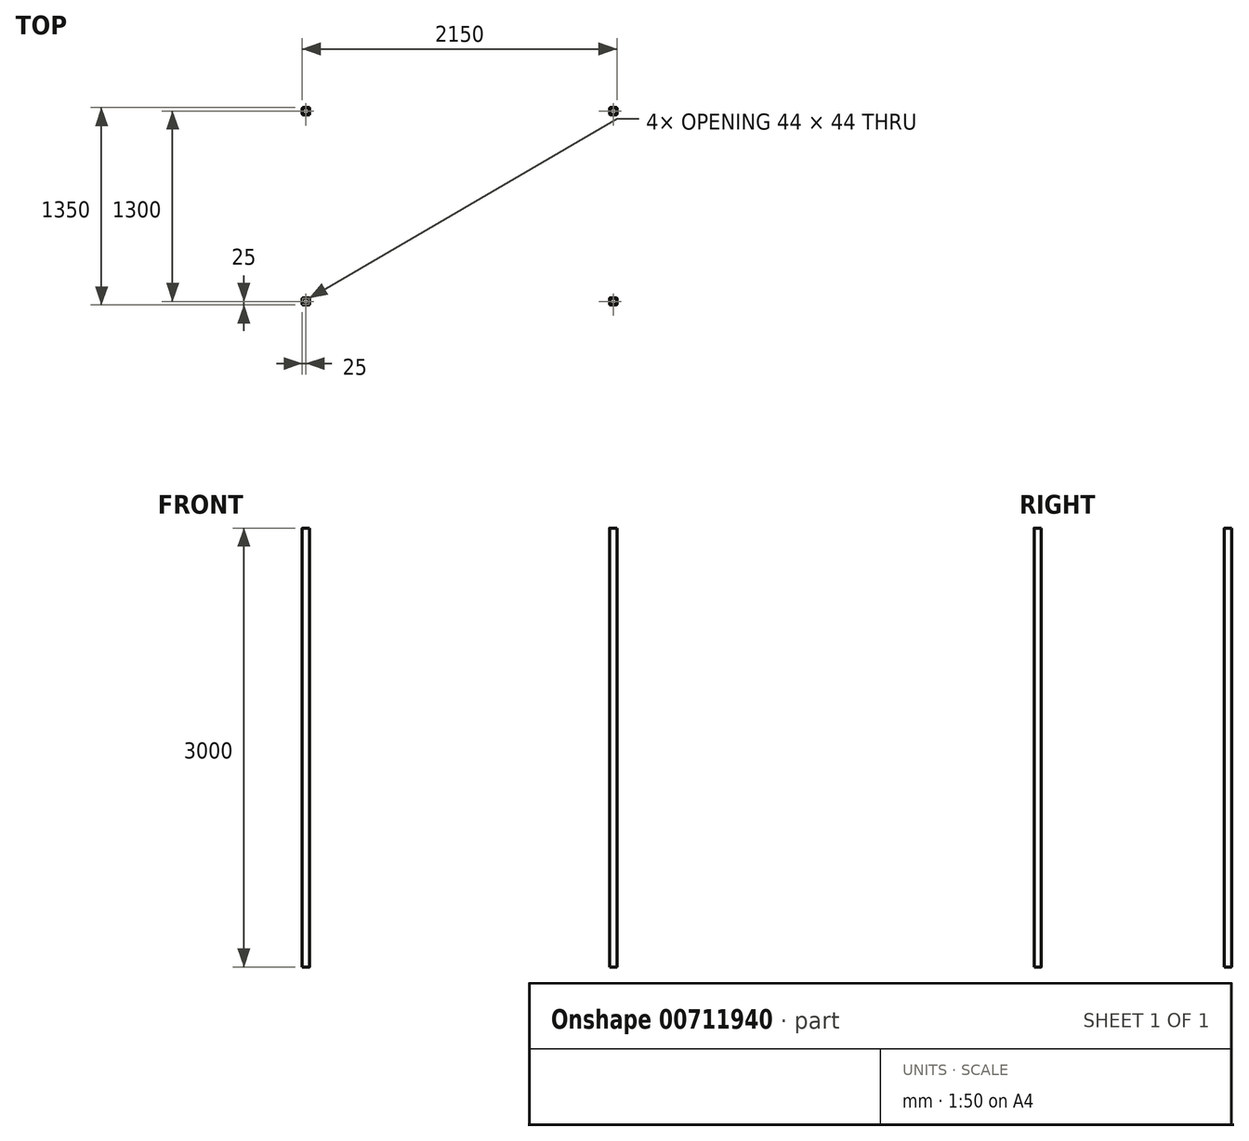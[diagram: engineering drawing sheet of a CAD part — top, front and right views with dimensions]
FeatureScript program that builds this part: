
annotation { "Feature Type Name" : "Feature", "Feature Type Description" : "" }
export const myFeature = defineFeature(function(context is Context, id is Id, definition is map)
    precondition{}
    {
        {
            var Q0;
            Q0=qCreatedBy(makeId("Top.planeOp"),FACE);
            var sketch = newSketch(context, id + "F0", { "sketchPlane" : qUnion([Q0])});
            skLineSegment(sketch, "E0.bottom", {"start": v(-1045, 1350) * mm, "end": v(-1005, 1350) * mm});
            skLineSegment(sketch, "E0.top", {"start": v(-1045, 1300) * mm, "end": v(-1005, 1300) * mm});
            skLineSegment(sketch, "E0.left", {"start": v(-1050, 1345) * mm, "end": v(-1050, 1305) * mm});
            skLineSegment(sketch, "E0.right", {"start": v(-1000, 1345) * mm, "end": v(-1000, 1305) * mm});
            skPoint(sketch, "E1.visualSharp", {"position": v(-1050, 1350) * mm});
            skArc(sketch, "E1.filletArc", {"start": v(-1045, 1350) * mm, "mid": v(-1048.54, 1348.54) * mm, "end": v(-1050, 1345) * mm});
            skPoint(sketch, "E2.visualSharp", {"position": v(-1000, 1350) * mm});
            skArc(sketch, "E2.filletArc", {"start": v(-1000, 1345) * mm, "mid": v(-1001.46, 1348.54) * mm, "end": v(-1005, 1350) * mm});
            skPoint(sketch, "E3.visualSharp", {"position": v(-1000, 1300) * mm});
            skArc(sketch, "E3.filletArc", {"start": v(-1005, 1300) * mm, "mid": v(-1001.46, 1301.46) * mm, "end": v(-1000, 1305) * mm});
            skPoint(sketch, "E4.visualSharp", {"position": v(-1050, 1300) * mm});
            skArc(sketch, "E4.filletArc", {"start": v(-1050, 1305) * mm, "mid": v(-1048.54, 1301.46) * mm, "end": v(-1045, 1300) * mm});
            skLineSegment(sketch, "E5.0", {"start": v(-1003, 1345) * mm, "end": v(-1003, 1305) * mm});
            skLineSegment(sketch, "E5.1", {"start": v(-1045, 1347) * mm, "end": v(-1005, 1347) * mm});
            skLineSegment(sketch, "E5.2", {"start": v(-1047, 1345) * mm, "end": v(-1047, 1305) * mm});
            skLineSegment(sketch, "E5.3", {"start": v(-1045, 1303) * mm, "end": v(-1005, 1303) * mm});
            skPoint(sketch, "E6.visualSharp", {"position": v(-1047, 1347) * mm});
            skArc(sketch, "E6.filletArc", {"start": v(-1045, 1347) * mm, "mid": v(-1046.41, 1346.41) * mm, "end": v(-1047, 1345) * mm});
            skPoint(sketch, "E7.visualSharp", {"position": v(-1003, 1347) * mm});
            skArc(sketch, "E7.filletArc", {"start": v(-1003, 1345) * mm, "mid": v(-1003.59, 1346.41) * mm, "end": v(-1005, 1347) * mm});
            skPoint(sketch, "E8.visualSharp", {"position": v(-1003, 1303) * mm});
            skArc(sketch, "E8.filletArc", {"start": v(-1005, 1303) * mm, "mid": v(-1003.59, 1303.59) * mm, "end": v(-1003, 1305) * mm});
            skPoint(sketch, "E9.visualSharp", {"position": v(-1047, 1303) * mm});
            skArc(sketch, "E9.filletArc", {"start": v(-1047, 1305) * mm, "mid": v(-1046.41, 1303.59) * mm, "end": v(-1045, 1303) * mm});
            skPoint(sketch, "E10.0.1.0", {"position": v(-1000, 0) * mm});
            skPoint(sketch, "E10.0.1.1", {"position": v(-1050, 0) * mm});
            skPoint(sketch, "E10.0.1.2", {"position": v(-1047, 3) * mm});
            skPoint(sketch, "E10.0.1.3", {"position": v(-1003, 3) * mm});
            skPoint(sketch, "E10.0.1.4", {"position": v(-1050, 50) * mm});
            skPoint(sketch, "E10.0.1.5", {"position": v(-1000, 50) * mm});
            skPoint(sketch, "E10.0.1.6", {"position": v(-1003, 47) * mm});
            skPoint(sketch, "E10.0.1.7", {"position": v(-1047, 47) * mm});
            skArc(sketch, "E10.0.1.8", {"start": v(-1005, 0) * mm, "mid": v(-1001.46, 1.46) * mm, "end": v(-1000, 5) * mm});
            skArc(sketch, "E10.0.1.9", {"start": v(-1050, 5) * mm, "mid": v(-1048.54, 1.46) * mm, "end": v(-1045, 0) * mm});
            skLineSegment(sketch, "E10.0.1.10", {"start": v(-1045, 3) * mm, "end": v(-1005, 3) * mm});
            skArc(sketch, "E10.0.1.11", {"start": v(-1005, 3) * mm, "mid": v(-1003.59, 3.59) * mm, "end": v(-1003, 5) * mm});
            skArc(sketch, "E10.0.1.12", {"start": v(-1047, 5) * mm, "mid": v(-1046.41, 3.59) * mm, "end": v(-1045, 3) * mm});
            skLineSegment(sketch, "E10.0.1.13", {"start": v(-1045, 0) * mm, "end": v(-1005, 0) * mm});
            skArc(sketch, "E10.0.1.14", {"start": v(-1000, 45) * mm, "mid": v(-1001.46, 48.54) * mm, "end": v(-1005, 50) * mm});
            skLineSegment(sketch, "E10.0.1.15", {"start": v(-1003, 45) * mm, "end": v(-1003, 5) * mm});
            skLineSegment(sketch, "E10.0.1.16", {"start": v(-1045, 47) * mm, "end": v(-1005, 47) * mm});
            skLineSegment(sketch, "E10.0.1.17", {"start": v(-1047, 45) * mm, "end": v(-1047, 5) * mm});
            skArc(sketch, "E10.0.1.18", {"start": v(-1045, 47) * mm, "mid": v(-1046.41, 46.41) * mm, "end": v(-1047, 45) * mm});
            skArc(sketch, "E10.0.1.19", {"start": v(-1003, 45) * mm, "mid": v(-1003.59, 46.41) * mm, "end": v(-1005, 47) * mm});
            skLineSegment(sketch, "E10.0.1.20", {"start": v(-1045, 50) * mm, "end": v(-1005, 50) * mm});
            skLineSegment(sketch, "E10.0.1.21", {"start": v(-1050, 45) * mm, "end": v(-1050, 5) * mm});
            skLineSegment(sketch, "E10.0.1.22", {"start": v(-1000, 45) * mm, "end": v(-1000, 5) * mm});
            skArc(sketch, "E10.0.1.23", {"start": v(-1045, 50) * mm, "mid": v(-1048.54, 48.54) * mm, "end": v(-1050, 45) * mm});
            skPoint(sketch, "E10.1.0.0", {"position": v(1100, 1300) * mm});
            skPoint(sketch, "E10.1.0.1", {"position": v(1050, 1300) * mm});
            skPoint(sketch, "E10.1.0.2", {"position": v(1053, 1303) * mm});
            skPoint(sketch, "E10.1.0.3", {"position": v(1097, 1303) * mm});
            skPoint(sketch, "E10.1.0.4", {"position": v(1050, 1350) * mm});
            skPoint(sketch, "E10.1.0.5", {"position": v(1100, 1350) * mm});
            skPoint(sketch, "E10.1.0.6", {"position": v(1097, 1347) * mm});
            skPoint(sketch, "E10.1.0.7", {"position": v(1053, 1347) * mm});
            skArc(sketch, "E10.1.0.8", {"start": v(1095, 1300) * mm, "mid": v(1098.54, 1301.46) * mm, "end": v(1100, 1305) * mm});
            skArc(sketch, "E10.1.0.9", {"start": v(1050, 1305) * mm, "mid": v(1051.46, 1301.46) * mm, "end": v(1055, 1300) * mm});
            skLineSegment(sketch, "E10.1.0.10", {"start": v(1055, 1303) * mm, "end": v(1095, 1303) * mm});
            skArc(sketch, "E10.1.0.11", {"start": v(1095, 1303) * mm, "mid": v(1096.41, 1303.59) * mm, "end": v(1097, 1305) * mm});
            skArc(sketch, "E10.1.0.12", {"start": v(1053, 1305) * mm, "mid": v(1053.59, 1303.59) * mm, "end": v(1055, 1303) * mm});
            skLineSegment(sketch, "E10.1.0.13", {"start": v(1055, 1300) * mm, "end": v(1095, 1300) * mm});
            skArc(sketch, "E10.1.0.14", {"start": v(1100, 1345) * mm, "mid": v(1098.54, 1348.54) * mm, "end": v(1095, 1350) * mm});
            skLineSegment(sketch, "E10.1.0.15", {"start": v(1097, 1345) * mm, "end": v(1097, 1305) * mm});
            skLineSegment(sketch, "E10.1.0.16", {"start": v(1055, 1347) * mm, "end": v(1095, 1347) * mm});
            skLineSegment(sketch, "E10.1.0.17", {"start": v(1053, 1345) * mm, "end": v(1053, 1305) * mm});
            skArc(sketch, "E10.1.0.18", {"start": v(1055, 1347) * mm, "mid": v(1053.59, 1346.41) * mm, "end": v(1053, 1345) * mm});
            skArc(sketch, "E10.1.0.19", {"start": v(1097, 1345) * mm, "mid": v(1096.41, 1346.41) * mm, "end": v(1095, 1347) * mm});
            skLineSegment(sketch, "E10.1.0.20", {"start": v(1055, 1350) * mm, "end": v(1095, 1350) * mm});
            skLineSegment(sketch, "E10.1.0.21", {"start": v(1050, 1345) * mm, "end": v(1050, 1305) * mm});
            skLineSegment(sketch, "E10.1.0.22", {"start": v(1100, 1345) * mm, "end": v(1100, 1305) * mm});
            skArc(sketch, "E10.1.0.23", {"start": v(1055, 1350) * mm, "mid": v(1051.46, 1348.54) * mm, "end": v(1050, 1345) * mm});
            skPoint(sketch, "E10.1.1.0", {"position": v(1100, 0) * mm});
            skPoint(sketch, "E10.1.1.1", {"position": v(1050, 0) * mm});
            skPoint(sketch, "E10.1.1.2", {"position": v(1053, 3) * mm});
            skPoint(sketch, "E10.1.1.3", {"position": v(1097, 3) * mm});
            skPoint(sketch, "E10.1.1.4", {"position": v(1050, 50) * mm});
            skPoint(sketch, "E10.1.1.5", {"position": v(1100, 50) * mm});
            skPoint(sketch, "E10.1.1.6", {"position": v(1097, 47) * mm});
            skPoint(sketch, "E10.1.1.7", {"position": v(1053, 47) * mm});
            skArc(sketch, "E10.1.1.8", {"start": v(1095, 0) * mm, "mid": v(1098.54, 1.46) * mm, "end": v(1100, 5) * mm});
            skArc(sketch, "E10.1.1.9", {"start": v(1050, 5) * mm, "mid": v(1051.46, 1.46) * mm, "end": v(1055, 0) * mm});
            skLineSegment(sketch, "E10.1.1.10", {"start": v(1055, 3) * mm, "end": v(1095, 3) * mm});
            skArc(sketch, "E10.1.1.11", {"start": v(1095, 3) * mm, "mid": v(1096.41, 3.59) * mm, "end": v(1097, 5) * mm});
            skArc(sketch, "E10.1.1.12", {"start": v(1053, 5) * mm, "mid": v(1053.59, 3.59) * mm, "end": v(1055, 3) * mm});
            skLineSegment(sketch, "E10.1.1.13", {"start": v(1055, 0) * mm, "end": v(1095, 0) * mm});
            skArc(sketch, "E10.1.1.14", {"start": v(1100, 45) * mm, "mid": v(1098.54, 48.54) * mm, "end": v(1095, 50) * mm});
            skLineSegment(sketch, "E10.1.1.15", {"start": v(1097, 45) * mm, "end": v(1097, 5) * mm});
            skLineSegment(sketch, "E10.1.1.16", {"start": v(1055, 47) * mm, "end": v(1095, 47) * mm});
            skLineSegment(sketch, "E10.1.1.17", {"start": v(1053, 45) * mm, "end": v(1053, 5) * mm});
            skArc(sketch, "E10.1.1.18", {"start": v(1055, 47) * mm, "mid": v(1053.59, 46.41) * mm, "end": v(1053, 45) * mm});
            skArc(sketch, "E10.1.1.19", {"start": v(1097, 45) * mm, "mid": v(1096.41, 46.41) * mm, "end": v(1095, 47) * mm});
            skLineSegment(sketch, "E10.1.1.20", {"start": v(1055, 50) * mm, "end": v(1095, 50) * mm});
            skLineSegment(sketch, "E10.1.1.21", {"start": v(1050, 45) * mm, "end": v(1050, 5) * mm});
            skLineSegment(sketch, "E10.1.1.22", {"start": v(1100, 45) * mm, "end": v(1100, 5) * mm});
            skArc(sketch, "E10.1.1.23", {"start": v(1055, 50) * mm, "mid": v(1051.46, 48.54) * mm, "end": v(1050, 45) * mm});
            skLineSegment(sketch, "E10.direction1", {"start": v(-1050, 1300) * mm, "end": v(1050, 1300) * mm, "construction": true});
            skLineSegment(sketch, "E10.direction2", {"start": v(-1050, 1300) * mm, "end": v(-1050, 0) * mm, "construction": true});
            skSolve(sketch);
        }
        {
            var Q0;
            Q0 = qSketchRegion(id + "F0", true);
            extrude(context, id + "F1", {"entities" : qUnion([Q0]), "depth" : 3000 * mm, "offsetDistance" : 25 * mm});
        }
    });
